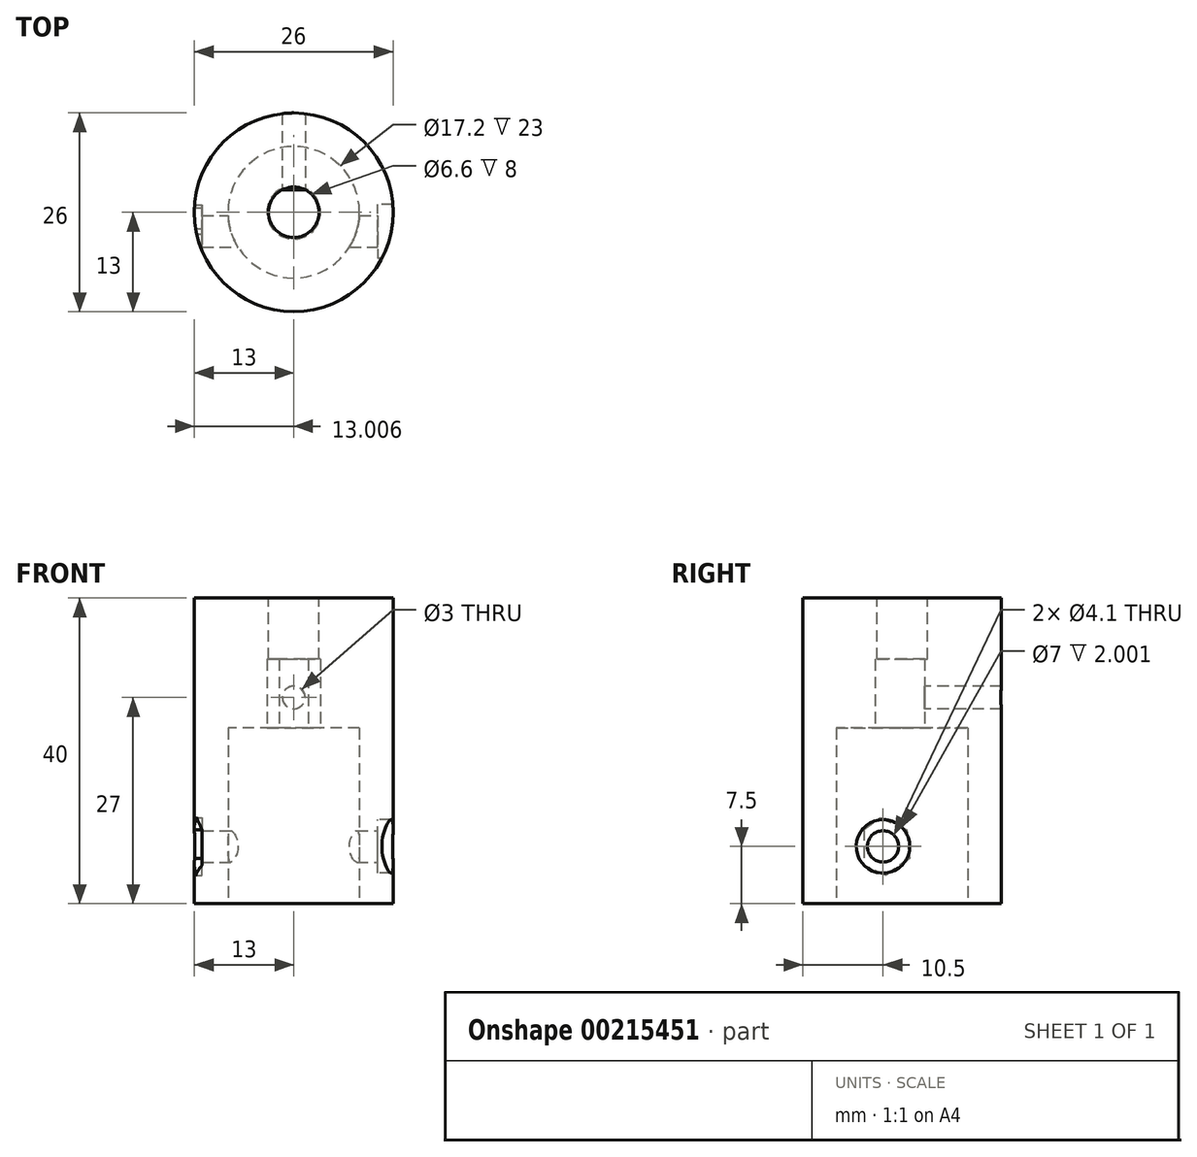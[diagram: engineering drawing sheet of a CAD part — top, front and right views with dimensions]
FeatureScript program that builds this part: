
annotation { "Feature Type Name" : "Feature", "Feature Type Description" : "" }
export const myFeature = defineFeature(function(context is Context, id is Id, definition is map)
    precondition{}
    {
        {
            var Q0;
            Q0=qCreatedBy(makeId("Top.planeOp"),FACE);
            var sketch = newSketch(context, id + "F0", { "sketchPlane" : qUnion([Q0])});
            skCircle(sketch, "E0", {"center": v(0, 0) * mm, "radius": 13 * mm});
            skSolve(sketch);
        }
        {
            var Q0;
            Q0=qCreatedBy(makeId("Top.planeOp"),FACE);
            cPlane(context, id + "F1", {"entities" : qUnion([Q0]), "cplaneType" : CPlaneType.OFFSET, "offset" : 20 * mm, "width" : 150 * mm, "height" : 150 * mm});
        }
        {
            var Q0;
            Q0=qCreatedBy(makeId("Top.planeOp"),FACE);
            cPlane(context, id + "F2", {"entities" : qUnion([Q0]), "cplaneType" : CPlaneType.OFFSET, "offset" : 20 * mm, "oppositeDirection" : true, "width" : 150 * mm, "height" : 150 * mm});
        }
        {
            var Q0;
            Q0=qCreatedBy(id+"F1.planeOp",FACE);
            var sketch = newSketch(context, id + "F3", { "sketchPlane" : qUnion([Q0])});
            skCircle(sketch, "E1", {"center": v(0, 0) * mm, "radius": 3.3 * mm});
            skSolve(sketch);
        }
        {
            var Q0;
            Q0=qCreatedBy(id+"F2.planeOp",FACE);
            var sketch = newSketch(context, id + "F4", { "sketchPlane" : qUnion([Q0])});
            skCircle(sketch, "E2", {"center": v(0, 0) * mm, "radius": 8.6 * mm});
            skSolve(sketch);
        }
        {
            var Q0;
            Q0=qSketchRegion(id+"F0",true);
            extrude(context, id + "F5", {"entities" : qUnion([Q0]), "depth" : 40 * mm, "symmetric" : true});
        }
        {
            var Q0;
            Q0=qSketchRegion(id+"F4",true);
            extrude(context, id + "F6", {"entities" : qUnion([Q0]), "operationType" : NewBodyOperationType.REMOVE, "depth" : 23 * mm});
        }
        {
            var Q0;
            Q0=qCreatedBy(makeId("Top.planeOp"),FACE);
            var sketch = newSketch(context, id + "F7", { "sketchPlane" : qUnion([Q0])});
            skLineSegment(sketch, "E3", {"start": v(0, 2.95) * mm, "end": v(-1.89, 2.95) * mm});
            skLineSegment(sketch, "E4", {"start": v(-1.89, 2.95) * mm, "end": v(1.89, 2.95) * mm});
            skArc(sketch, "E5", {"start": v(-1.89, 2.95) * mm, "mid": v(0, -3.5) * mm, "end": v(1.89, 2.95) * mm});
            skSolve(sketch);
        }
        {
            var Q0;
            Q0=qSketchRegion(id+"F3",true);
            extrude(context, id + "F8", {"entities" : qUnion([Q0]), "operationType" : NewBodyOperationType.REMOVE, "oppositeDirection" : true, "depth" : 8 * mm});
        }
        {
            var Q0;
            Q0=qSketchRegion(id+"F7",true);
            extrude(context, id + "F9", {"entities" : qUnion([Q0]), "operationType" : NewBodyOperationType.REMOVE, "depth" : 12 * mm});
        }
        {
            var Q0;
            Q0=qCreatedBy(makeId("Right.planeOp"),FACE);
            var sketch = newSketch(context, id + "F10", { "sketchPlane" : qUnion([Q0])});
            skCircle(sketch, "E6", {"center": v(-2.5, -12.5) * mm, "radius": 2.05 * mm});
            skSolve(sketch);
        }
        {
            var Q0;
            Q0=qSketchRegion(id+"F10",true);
            extrude(context, id + "F11", {"entities" : qUnion([Q0]), "operationType" : NewBodyOperationType.REMOVE, "oppositeDirection" : true, "depth" : 30 * mm, "symmetric" : true});
        }
        {
            var Q0;
            Q0=qCreatedBy(makeId("Front.planeOp"),FACE);
            var sketch = newSketch(context, id + "F12", { "sketchPlane" : qUnion([Q0])});
            skCircle(sketch, "E7", {"center": v(0, 7) * mm, "radius": 1.5 * mm});
            skSolve(sketch);
        }
        {
            var Q0;
            Q0=qSketchRegion(id+"F12",true);
            extrude(context, id + "F13", {"entities" : qUnion([Q0]), "operationType" : NewBodyOperationType.REMOVE, "oppositeDirection" : true, "depth" : 25 * mm});
        }
        {
            var Q0;
            Q0=qCreatedBy(makeId("Right.planeOp"),FACE);
            cPlane(context, id + "F14", {"entities" : qUnion([Q0]), "cplaneType" : CPlaneType.OFFSET, "offset" : 11 * mm, "width" : 150 * mm, "height" : 150 * mm});
        }
        {
            var Q0;
            Q0=qCreatedBy(id+"F14.planeOp",FACE);
            var sketch = newSketch(context, id + "F15", { "sketchPlane" : qUnion([Q0])});
            skCircle(sketch, "E8", {"center": v(-2.5, -12.5) * mm, "radius": 3.5 * mm});
            skSolve(sketch);
        }
        {
            var Q0;
            Q0=qSketchRegion(id+"F15",true);
            extrude(context, id + "F16", {"entities" : qUnion([Q0]), "operationType" : NewBodyOperationType.REMOVE, "depth" : 5 * mm});
        }
        {
            var Q0;
            Q0=qCreatedBy(makeId("Right.planeOp"),FACE);
            cPlane(context, id + "F17", {"entities" : qUnion([Q0]), "cplaneType" : CPlaneType.OFFSET, "offset" : 12 * mm, "oppositeDirection" : true, "width" : 150 * mm, "height" : 150 * mm});
        }
        {
            var Q0;
            Q0=qCreatedBy(id+"F17.planeOp",FACE);
            var sketch = newSketch(context, id + "F18", { "sketchPlane" : qUnion([Q0])});
            skCircle(sketch, "E9.cCircle", {"center": v(-2.5, -12.5) * mm, "radius": 3.8 * mm, "construction": true});
            skLineSegment(sketch, "E9.0", {"start": v(-5.6, -14.68) * mm, "end": v(-5.95, -10.9) * mm});
            skLineSegment(sketch, "E9.1", {"start": v(-5.95, -10.9) * mm, "end": v(-2.84, -8.71) * mm});
            skLineSegment(sketch, "E9.2", {"start": v(-2.84, -8.71) * mm, "end": v(0.6, -10.32) * mm});
            skLineSegment(sketch, "E9.3", {"start": v(0.6, -10.32) * mm, "end": v(0.95, -14.1) * mm});
            skLineSegment(sketch, "E9.4", {"start": v(0.95, -14.1) * mm, "end": v(-2.16, -16.29) * mm});
            skLineSegment(sketch, "E9.5", {"start": v(-2.16, -16.29) * mm, "end": v(-5.6, -14.68) * mm});
            skSolve(sketch);
        }
        {
            var Q0;
            Q0=qSketchRegion(id+"F18",true);
            extrude(context, id + "F19", {"entities" : qUnion([Q0]), "operationType" : NewBodyOperationType.REMOVE, "oppositeDirection" : true, "depth" : 3 * mm});
        }
    });
